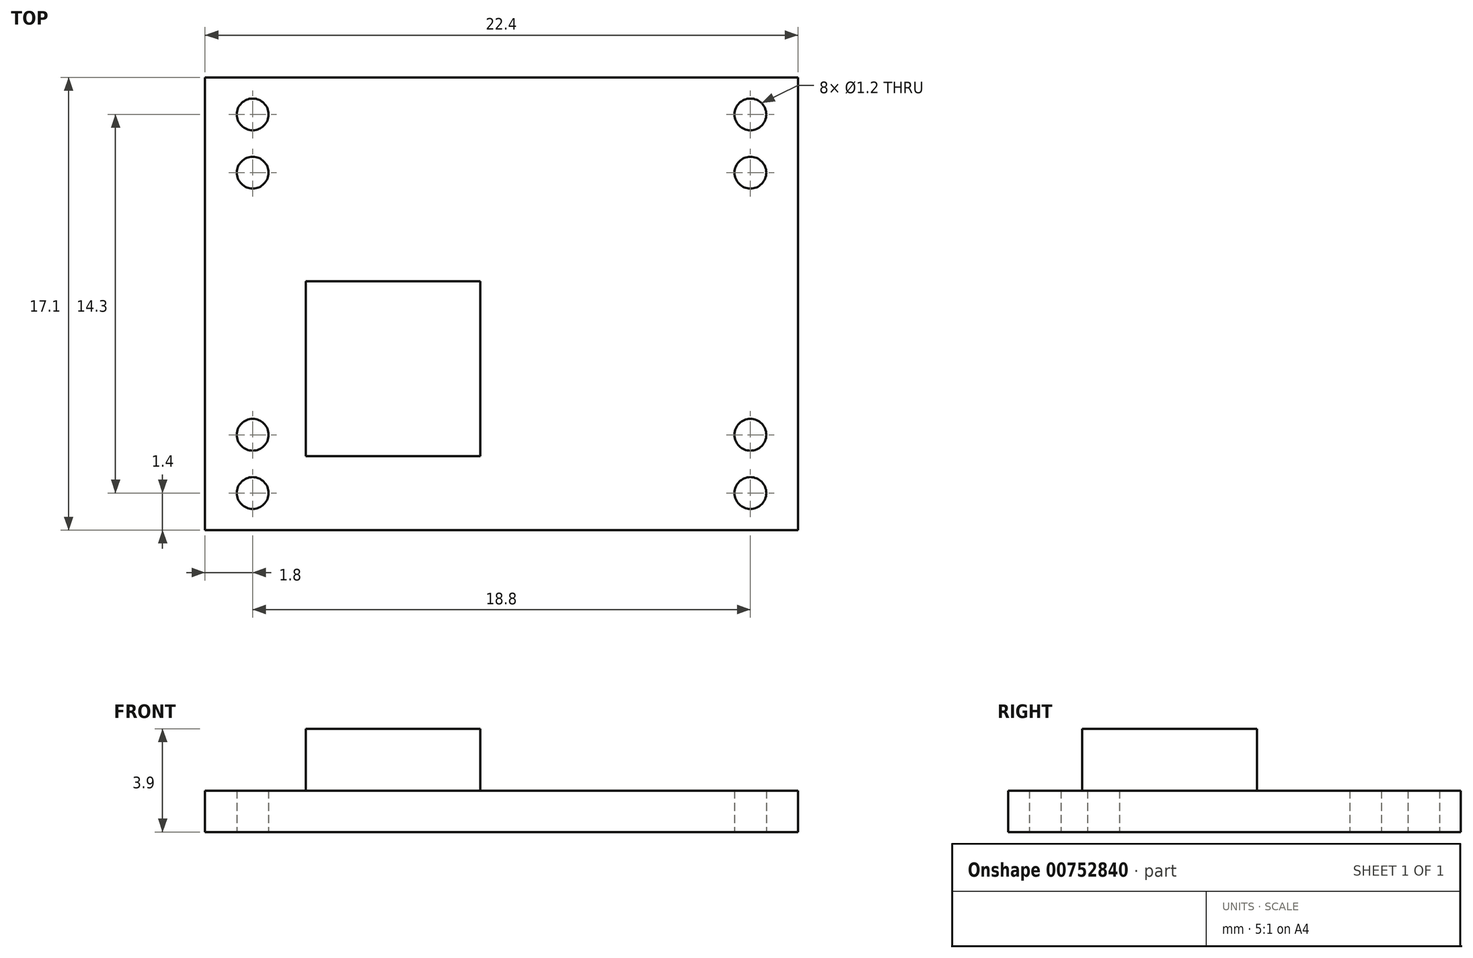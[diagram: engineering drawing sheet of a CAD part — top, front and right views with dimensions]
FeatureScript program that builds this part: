
annotation { "Feature Type Name" : "Feature", "Feature Type Description" : "" }
export const myFeature = defineFeature(function(context is Context, id is Id, definition is map)
    precondition{}
    {
        {
            var Q0;
            Q0=qCreatedBy(makeId("Top.planeOp"),FACE);
            var sketch = newSketch(context, id + "F0", { "sketchPlane" : qUnion([Q0])});
            skLineSegment(sketch, "E0.bottom", {"start": v(-22.4, 17.1) * mm, "end": v(0, 17.1) * mm});
            skLineSegment(sketch, "E0.top", {"start": v(-22.4, 0) * mm, "end": v(0, 0) * mm});
            skLineSegment(sketch, "E0.left", {"start": v(-22.4, 17.1) * mm, "end": v(-22.4, 0) * mm});
            skLineSegment(sketch, "E0.right", {"start": v(0, 17.1) * mm, "end": v(0, 0) * mm});
            skCircle(sketch, "E1", {"center": v(-1.8, 15.7) * mm, "radius": 0.6 * mm});
            skCircle(sketch, "E2", {"center": v(-1.8, 13.5) * mm, "radius": 0.6 * mm});
            skCircle(sketch, "E3", {"center": v(-1.8, 3.6) * mm, "radius": 0.6 * mm});
            skCircle(sketch, "E4", {"center": v(-1.8, 1.4) * mm, "radius": 0.6 * mm});
            skCircle(sketch, "E5", {"center": v(-20.6, 15.7) * mm, "radius": 0.6 * mm});
            skCircle(sketch, "E6", {"center": v(-20.6, 13.5) * mm, "radius": 0.6 * mm});
            skCircle(sketch, "E7", {"center": v(-20.6, 3.6) * mm, "radius": 0.6 * mm});
            skCircle(sketch, "E8", {"center": v(-20.6, 1.4) * mm, "radius": 0.6 * mm});
            skSolve(sketch);
        }
        {
            var Q0;
            Q0=makeQuery(id+"F0.imprint","IMPRINT",FACE,{"disambiguationData":[TD([[makeQuery(id+"F0.imprint","IMPRINT",EDGE,{"derivedFrom":sQuery(id+"F0.wireOp",EDGE,"E0.bottom")}),-1.0]])]});
            extrude(context, id + "F1", {"entities" : qUnion([Q0]), "depth" : 1.56 * mm, "offsetDistance" : 25 * mm});
        }
        {
            var Q0;
            Q0=makeQuery(id+"F1.opExtrude","CAP_FACE",FACE,{"disambiguationData":[OSD([sQuery(id+"F0.wireOp",EDGE,"E0.bottom"),sQuery(id+"F0.wireOp",EDGE,"E0.top"),sQuery(id+"F0.wireOp",EDGE,"E0.left"),sQuery(id+"F0.wireOp",EDGE,"E0.right"),sQuery(id+"F0.wireOp",EDGE,"E1"),sQuery(id+"F0.wireOp",EDGE,"E2"),sQuery(id+"F0.wireOp",EDGE,"E3"),sQuery(id+"F0.wireOp",EDGE,"E4"),sQuery(id+"F0.wireOp",EDGE,"E5"),sQuery(id+"F0.wireOp",EDGE,"E6"),sQuery(id+"F0.wireOp",EDGE,"E7"),sQuery(id+"F0.wireOp",EDGE,"E8")])],"isStart":false});
            var sketch = newSketch(context, id + "F2", { "sketchPlane" : qUnion([Q0])});
            skLineSegment(sketch, "E9.bottom", {"start": v(-18.6, 9.4) * mm, "end": v(-12, 9.4) * mm});
            skLineSegment(sketch, "E9.top", {"start": v(-18.6, 2.8) * mm, "end": v(-12, 2.8) * mm});
            skLineSegment(sketch, "E9.left", {"start": v(-18.6, 9.4) * mm, "end": v(-18.6, 2.8) * mm});
            skLineSegment(sketch, "E9.right", {"start": v(-12, 9.4) * mm, "end": v(-12, 2.8) * mm});
            skSolve(sketch);
        }
        {
            var Q0;
            Q0 = qSketchRegion(id + "F2", true);
            extrude(context, id + "F3", {"entities" : qUnion([Q0]), "operationType" : NewBodyOperationType.ADD, "depth" : 2.34 * mm, "offsetDistance" : 25 * mm});
        }
    });
